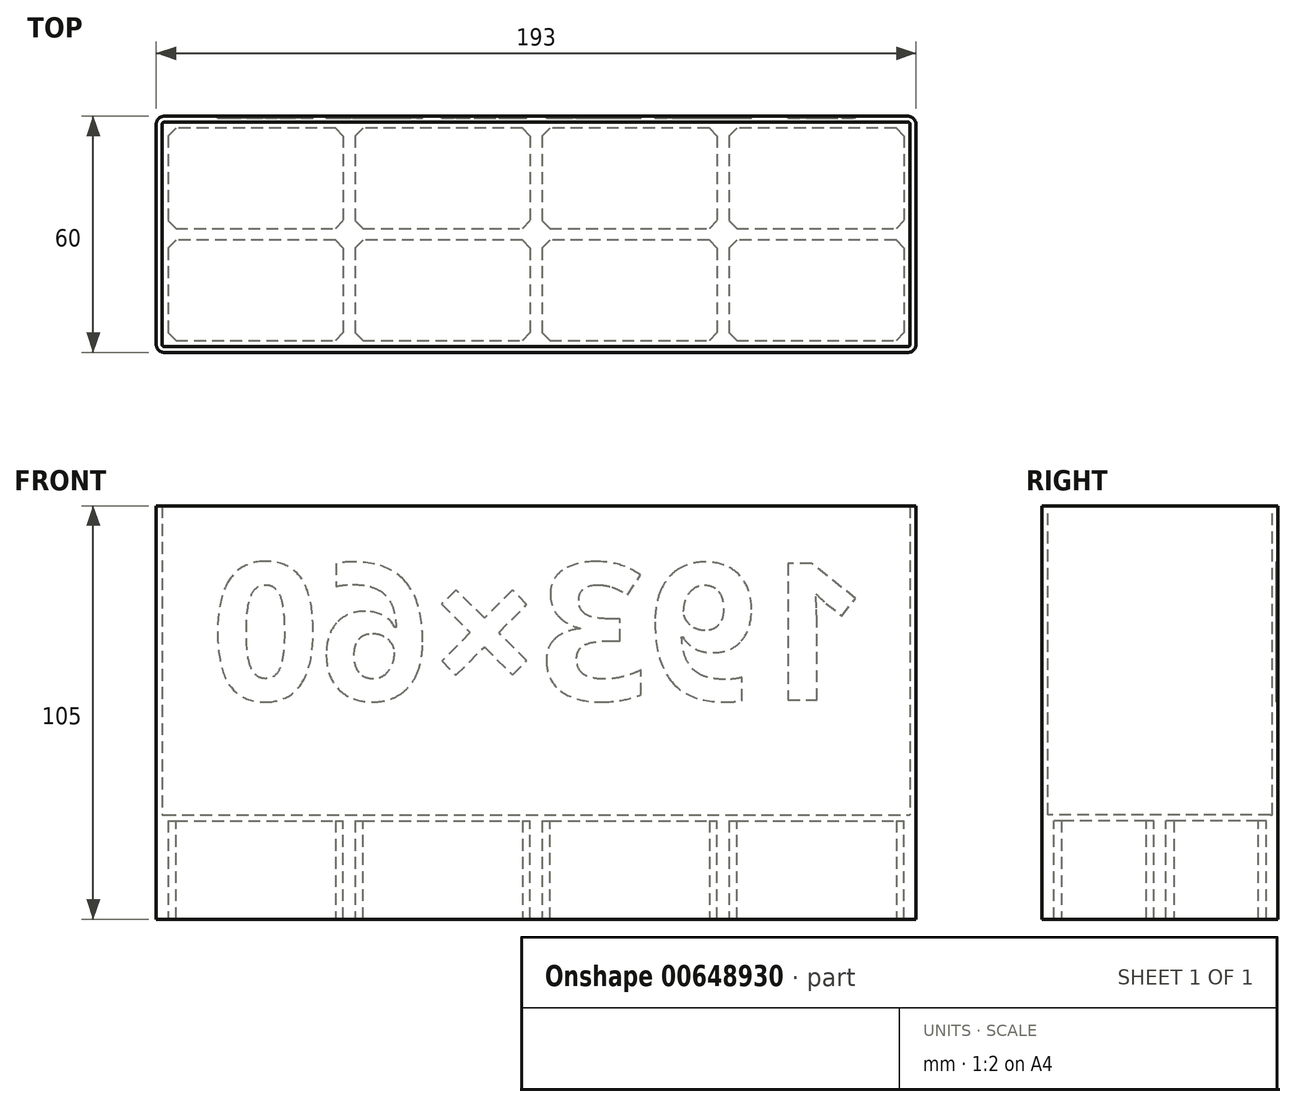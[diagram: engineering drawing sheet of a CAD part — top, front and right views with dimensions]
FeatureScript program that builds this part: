
annotation { "Feature Type Name" : "Feature", "Feature Type Description" : "" }
export const myFeature = defineFeature(function(context is Context, id is Id, definition is map)
    precondition{}
    {
        {
            assignVariable(context, id + "F0", {"variableType" : VariableType.LENGTH, "name" : "t", "lengthValue" : 1.5 * mm});
        }
        {
            assignVariable(context, id + "F1", {"variableType" : VariableType.LENGTH, "name" : "gap", "lengthValue" : 0.5 * mm});
        }
        {
            var Q0;
            Q0=qCreatedBy(makeId("Top.planeOp"),FACE);
            var sketch = newSketch(context, id + "F2", { "sketchPlane" : qUnion([Q0])});
            skLineSegment(sketch, "E0.bottom", {"start": v(-95, 28.5) * mm, "end": v(95, 28.5) * mm, "construction": true});
            skLineSegment(sketch, "E0.top", {"start": v(-95, -28.5) * mm, "end": v(95, -28.5) * mm, "construction": true});
            skLineSegment(sketch, "E0.left", {"start": v(-95, 28.5) * mm, "end": v(-95, -28.5) * mm, "construction": true});
            skLineSegment(sketch, "E0.right", {"start": v(95, 28.5) * mm, "end": v(95, -28.5) * mm, "construction": true});
            skPoint(sketch, "E0.middle", {"position": v(0, 0) * mm});
            skLineSegment(sketch, "E1.0", {"start": v(-96.5, 30) * mm, "end": v(96.5, 30) * mm});
            skLineSegment(sketch, "E1.1", {"start": v(-96.5, 30) * mm, "end": v(-96.5, -30) * mm});
            skLineSegment(sketch, "E1.2", {"start": v(-96.5, -30) * mm, "end": v(96.5, -30) * mm});
            skLineSegment(sketch, "E1.3", {"start": v(96.5, 30) * mm, "end": v(96.5, -30) * mm});
            skSolve(sketch);
        }
        {
            var Q0;
            Q0 = qSketchRegion(id + "F2", true);
            extrude(context, id + "F3", {"entities" : qUnion([Q0]), "depth" : 80 * mm, "offsetDistance" : 25 * mm});
        }
        {
            var Q0;
            Q0=makeQuery(id+"F3.opExtrude","CAP_FACE",FACE,{"disambiguationData":[OSD([sQuery(id+"F2.wireOp",EDGE,"E1.0"),sQuery(id+"F2.wireOp",EDGE,"E1.1"),sQuery(id+"F2.wireOp",EDGE,"E1.2"),sQuery(id+"F2.wireOp",EDGE,"E1.3")])],"isStart":true});
            var sketch = newSketch(context, id + "F4", { "sketchPlane" : qUnion([Q0])});
            skLineSegment(sketch, "E2.0", {"start": v(-95, 28.5) * mm, "end": v(-47.5, 28.5) * mm, "construction": true});
            skLineSegment(sketch, "E2.1", {"start": v(-95, -28.5) * mm, "end": v(-95, 0) * mm, "construction": true});
            skLineSegment(sketch, "E2.2", {"start": v(-95, -28.5) * mm, "end": v(95, -28.5) * mm, "construction": true});
            skLineSegment(sketch, "E2.3", {"start": v(95, -28.5) * mm, "end": v(95, 28.5) * mm, "construction": true});
            skLineSegment(sketch, "E3", {"start": v(0, 0) * mm, "end": v(0, 28.5) * mm, "construction": true});
            skLineSegment(sketch, "E4", {"start": v(0, 0) * mm, "end": v(-47.5, 0) * mm, "construction": true});
            skLineSegment(sketch, "E5", {"start": v(-47.5, 0) * mm, "end": v(-47.5, 28.5) * mm, "construction": true});
            skLineSegment(sketch, "E6", {"start": v(-47.5, 0) * mm, "end": v(-95, 0) * mm, "construction": true});
            skLineSegment(sketch, "E7", {"start": v(-47.5, 28.5) * mm, "end": v(95, 28.5) * mm, "construction": true});
            skLineSegment(sketch, "E8", {"start": v(-95, 0) * mm, "end": v(-95, 28.5) * mm, "construction": true});
            skLineSegment(sketch, "E9.0", {"start": v(-93.5, 27) * mm, "end": v(-49, 27) * mm});
            skLineSegment(sketch, "E9.1", {"start": v(-93.5, 1.5) * mm, "end": v(-93.5, 27) * mm});
            skLineSegment(sketch, "E9.2", {"start": v(-49, 1.5) * mm, "end": v(-93.5, 1.5) * mm});
            skLineSegment(sketch, "E9.3", {"start": v(-49, 1.5) * mm, "end": v(-49, 27) * mm});
            skLineSegment(sketch, "E10.0.1.0", {"start": v(-93.5, -1.5) * mm, "end": v(-49, -1.5) * mm});
            skLineSegment(sketch, "E10.0.1.1", {"start": v(-93.5, -27) * mm, "end": v(-93.5, -1.5) * mm});
            skLineSegment(sketch, "E10.0.1.2", {"start": v(-49, -27) * mm, "end": v(-93.5, -27) * mm});
            skLineSegment(sketch, "E10.0.1.3", {"start": v(-49, -27) * mm, "end": v(-49, -1.5) * mm});
            skLineSegment(sketch, "E10.1.0.0", {"start": v(-46, 27) * mm, "end": v(-1.5, 27) * mm});
            skLineSegment(sketch, "E10.1.0.1", {"start": v(-46, 1.5) * mm, "end": v(-46, 27) * mm});
            skLineSegment(sketch, "E10.1.0.2", {"start": v(-1.5, 1.5) * mm, "end": v(-46, 1.5) * mm});
            skLineSegment(sketch, "E10.1.0.3", {"start": v(-1.5, 1.5) * mm, "end": v(-1.5, 27) * mm});
            skLineSegment(sketch, "E10.1.1.0", {"start": v(-46, -1.5) * mm, "end": v(-1.5, -1.5) * mm});
            skLineSegment(sketch, "E10.1.1.1", {"start": v(-46, -27) * mm, "end": v(-46, -1.5) * mm});
            skLineSegment(sketch, "E10.1.1.2", {"start": v(-1.5, -27) * mm, "end": v(-46, -27) * mm});
            skLineSegment(sketch, "E10.1.1.3", {"start": v(-1.5, -27) * mm, "end": v(-1.5, -1.5) * mm});
            skLineSegment(sketch, "E10.2.0.0", {"start": v(1.5, 27) * mm, "end": v(46, 27) * mm});
            skLineSegment(sketch, "E10.2.0.1", {"start": v(1.5, 1.5) * mm, "end": v(1.5, 27) * mm});
            skLineSegment(sketch, "E10.2.0.2", {"start": v(46, 1.5) * mm, "end": v(1.5, 1.5) * mm});
            skLineSegment(sketch, "E10.2.0.3", {"start": v(46, 1.5) * mm, "end": v(46, 27) * mm});
            skLineSegment(sketch, "E10.2.1.0", {"start": v(1.5, -1.5) * mm, "end": v(46, -1.5) * mm});
            skLineSegment(sketch, "E10.2.1.1", {"start": v(1.5, -27) * mm, "end": v(1.5, -1.5) * mm});
            skLineSegment(sketch, "E10.2.1.2", {"start": v(46, -27) * mm, "end": v(1.5, -27) * mm});
            skLineSegment(sketch, "E10.2.1.3", {"start": v(46, -27) * mm, "end": v(46, -1.5) * mm});
            skLineSegment(sketch, "E10.3.0.0", {"start": v(49, 27) * mm, "end": v(93.5, 27) * mm});
            skLineSegment(sketch, "E10.3.0.1", {"start": v(49, 1.5) * mm, "end": v(49, 27) * mm});
            skLineSegment(sketch, "E10.3.0.2", {"start": v(93.5, 1.5) * mm, "end": v(49, 1.5) * mm});
            skLineSegment(sketch, "E10.3.0.3", {"start": v(93.5, 1.5) * mm, "end": v(93.5, 27) * mm});
            skLineSegment(sketch, "E10.3.1.0", {"start": v(49, -1.5) * mm, "end": v(93.5, -1.5) * mm});
            skLineSegment(sketch, "E10.3.1.1", {"start": v(49, -27) * mm, "end": v(49, -1.5) * mm});
            skLineSegment(sketch, "E10.3.1.2", {"start": v(93.5, -27) * mm, "end": v(49, -27) * mm});
            skLineSegment(sketch, "E10.3.1.3", {"start": v(93.5, -27) * mm, "end": v(93.5, -1.5) * mm});
            skLineSegment(sketch, "E10.direction1", {"start": v(-93.5, 1.5) * mm, "end": v(-46, 1.5) * mm, "construction": true});
            skLineSegment(sketch, "E10.direction2", {"start": v(-93.5, 1.5) * mm, "end": v(-93.5, -27) * mm, "construction": true});
            skLineSegment(sketch, "E11.bottom", {"start": v(-96.5, 30) * mm, "end": v(96.5, 30) * mm});
            skLineSegment(sketch, "E11.top", {"start": v(-96.5, -30) * mm, "end": v(96.5, -30) * mm});
            skLineSegment(sketch, "E11.left", {"start": v(-96.5, 30) * mm, "end": v(-96.5, -30) * mm});
            skLineSegment(sketch, "E11.right", {"start": v(96.5, 30) * mm, "end": v(96.5, -30) * mm});
            skSolve(sketch);
        }
        {
            var Q0;
            Q0=makeQuery(id+"F3.opExtrude","SWEPT_EDGE",EDGE,{"disambiguationData":[OSD([sQuery(id+"F2.wireOp",EDGE,"E1.1"),sQuery(id+"F2.wireOp",EDGE,"E1.2")])]});
            var Q1;
            Q1=makeQuery(id+"F3.opExtrude","SWEPT_EDGE",EDGE,{"disambiguationData":[OSD([sQuery(id+"F2.wireOp",EDGE,"E1.2"),sQuery(id+"F2.wireOp",EDGE,"E1.3")])]});
            var Q2;
            Q2=makeQuery(id+"F3.opExtrude","SWEPT_EDGE",EDGE,{"disambiguationData":[OSD([sQuery(id+"F2.wireOp",EDGE,"E1.0"),sQuery(id+"F2.wireOp",EDGE,"E1.3")])]});
            var Q3;
            Q3=makeQuery(id+"F3.opExtrude","SWEPT_EDGE",EDGE,{"disambiguationData":[OSD([sQuery(id+"F2.wireOp",EDGE,"E1.0"),sQuery(id+"F2.wireOp",EDGE,"E1.1")])]});
            fillet(context, id + "F5", {"entities" : qUnion([Q0, Q1, Q2, Q3]), "tangentPropagation" : true, "radius" : getVariable(context, 't') + getVariable(context, 'gap'), "defaultsChanged" : false, "vertexSettings" : [], "allowEdgeOverflow" : false});
        }
        {
            var Q0;
            Q0=makeQuery(id+"F3.opExtrude","CAP_FACE",FACE,{"disambiguationData":[OSD([sQuery(id+"F2.wireOp",EDGE,"E1.0"),sQuery(id+"F2.wireOp",EDGE,"E1.1"),sQuery(id+"F2.wireOp",EDGE,"E1.2"),sQuery(id+"F2.wireOp",EDGE,"E1.3")])],"isStart":false});
            shell(context, id + "F6", {"entities" : qUnion([Q0]), "thickness" : getVariable(context, 't')});
        }
        {
            var Q0;
            Q0 = qSketchRegion(id + "F4", true);
            extrude(context, id + "F7", {"entities" : qUnion([Q0]), "operationType" : NewBodyOperationType.ADD, "depth" : 25 * mm, "offsetDistance" : 25 * mm});
        }
        {
            var Q0;
            Q0=makeQuery(id+"F7.boolean.opBoolean","MERGE",FACE,{"derivedFrom":[makeQuery(id+"F3.opExtrude","SWEPT_FACE",FACE,{"disambiguationData":[OSD([sQuery(id+"F2.wireOp",EDGE,"E1.0")])]}),makeQuery(id+"F7.opExtrude","SWEPT_FACE",FACE,{"disambiguationData":[OSD([sQuery(id+"F4.wireOp",EDGE,"E11.top")])]})]});
            var sketch = newSketch(context, id + "F8", { "sketchPlane" : qUnion([Q0])});
            skText(sketch, "E12", { "text": "193×60", "fontName": "NotoSans-Bold.ttf"});
            const initialGuessF8  = {"E12": [-0.08406, 0.03067, 1, 0, 0.035]};
            skSetInitialGuess(sketch, initialGuessF8);
            skSolve(sketch);
        }
        {
            var Q0;
            Q0 = qSketchRegion(id + "F8", true);
            extrude(context, id + "F9", {"entities" : qUnion([Q0]), "operationType" : NewBodyOperationType.REMOVE, "oppositeDirection" : true, "depth" : getVariable(context, 't') * (1 / 3), "offsetDistance" : 25 * mm});
        }
        {
            var Q0;
            Q0=makeQuery(id+"F7.opExtrude","SWEPT_EDGE",EDGE,{"disambiguationData":[OSD([sQuery(id+"F4.wireOp",EDGE,"E11.bottom"),sQuery(id+"F4.wireOp",EDGE,"E11.left")])]});
            var Q1;
            Q1=makeQuery(id+"F7.opExtrude","SWEPT_EDGE",EDGE,{"disambiguationData":[OSD([sQuery(id+"F4.wireOp",EDGE,"E11.top"),sQuery(id+"F4.wireOp",EDGE,"E11.left")])]});
            var Q2;
            Q2=makeQuery(id+"F7.opExtrude","SWEPT_EDGE",EDGE,{"disambiguationData":[OSD([sQuery(id+"F4.wireOp",EDGE,"E11.bottom"),sQuery(id+"F4.wireOp",EDGE,"E11.right")])]});
            var Q3;
            Q3=makeQuery(id+"F7.opExtrude","SWEPT_EDGE",EDGE,{"disambiguationData":[OSD([sQuery(id+"F4.wireOp",EDGE,"E11.top"),sQuery(id+"F4.wireOp",EDGE,"E11.right")])]});
            fillet(context, id + "F10", {"entities" : qUnion([Q0, Q1, Q2, Q3]), "tangentPropagation" : true, "radius" : getVariable(context, 't') + getVariable(context, 'gap'), "defaultsChanged" : false, "vertexSettings" : [], "allowEdgeOverflow" : false});
        }
        {
            var Q0;
            Q0=makeQuery(id+"F7.opExtrude","SWEPT_EDGE",EDGE,{"disambiguationData":[OSD([sQuery(id+"F4.wireOp",EDGE,"E9.0"),sQuery(id+"F4.wireOp",EDGE,"E9.1")])]});
            var Q1;
            Q1=makeQuery(id+"F7.opExtrude","SWEPT_EDGE",EDGE,{"disambiguationData":[OSD([sQuery(id+"F4.wireOp",EDGE,"E9.0"),sQuery(id+"F4.wireOp",EDGE,"E9.3")])]});
            var Q2;
            Q2=makeQuery(id+"F7.opExtrude","SWEPT_EDGE",EDGE,{"disambiguationData":[OSD([sQuery(id+"F4.wireOp",EDGE,"E10.1.0.0"),sQuery(id+"F4.wireOp",EDGE,"E10.1.0.3")])]});
            var Q3;
            Q3=makeQuery(id+"F7.opExtrude","SWEPT_EDGE",EDGE,{"disambiguationData":[OSD([sQuery(id+"F4.wireOp",EDGE,"E10.0.1.0"),sQuery(id+"F4.wireOp",EDGE,"E10.0.1.3")])]});
            var Q4;
            Q4=makeQuery(id+"F7.opExtrude","SWEPT_EDGE",EDGE,{"disambiguationData":[OSD([sQuery(id+"F4.wireOp",EDGE,"E10.1.1.0"),sQuery(id+"F4.wireOp",EDGE,"E10.1.1.3")])]});
            var Q5;
            Q5=makeQuery(id+"F7.opExtrude","SWEPT_EDGE",EDGE,{"disambiguationData":[OSD([sQuery(id+"F4.wireOp",EDGE,"E10.2.0.0"),sQuery(id+"F4.wireOp",EDGE,"E10.2.0.3")])]});
            var Q6;
            Q6=makeQuery(id+"F7.opExtrude","SWEPT_EDGE",EDGE,{"disambiguationData":[OSD([sQuery(id+"F4.wireOp",EDGE,"E10.2.1.0"),sQuery(id+"F4.wireOp",EDGE,"E10.2.1.3")])]});
            var Q7;
            Q7=makeQuery(id+"F7.opExtrude","SWEPT_EDGE",EDGE,{"disambiguationData":[OSD([sQuery(id+"F4.wireOp",EDGE,"E10.3.1.0"),sQuery(id+"F4.wireOp",EDGE,"E10.3.1.3")])]});
            var Q8;
            Q8=makeQuery(id+"F7.opExtrude","SWEPT_EDGE",EDGE,{"disambiguationData":[OSD([sQuery(id+"F4.wireOp",EDGE,"E10.3.0.0"),sQuery(id+"F4.wireOp",EDGE,"E10.3.0.3")])]});
            var Q9;
            Q9=makeQuery(id+"F7.opExtrude","SWEPT_EDGE",EDGE,{"disambiguationData":[OSD([sQuery(id+"F4.wireOp",EDGE,"E9.1"),sQuery(id+"F4.wireOp",EDGE,"E9.2")])]});
            var Q10;
            Q10=makeQuery(id+"F7.opExtrude","SWEPT_EDGE",EDGE,{"disambiguationData":[OSD([sQuery(id+"F4.wireOp",EDGE,"E10.0.1.1"),sQuery(id+"F4.wireOp",EDGE,"E10.0.1.2")])]});
            var Q11;
            Q11=makeQuery(id+"F7.opExtrude","SWEPT_EDGE",EDGE,{"disambiguationData":[OSD([sQuery(id+"F4.wireOp",EDGE,"E10.1.1.1"),sQuery(id+"F4.wireOp",EDGE,"E10.1.1.2")])]});
            var Q12;
            Q12=makeQuery(id+"F7.opExtrude","SWEPT_EDGE",EDGE,{"disambiguationData":[OSD([sQuery(id+"F4.wireOp",EDGE,"E10.2.1.1"),sQuery(id+"F4.wireOp",EDGE,"E10.2.1.2")])]});
            var Q13;
            Q13=makeQuery(id+"F7.opExtrude","SWEPT_EDGE",EDGE,{"disambiguationData":[OSD([sQuery(id+"F4.wireOp",EDGE,"E10.3.1.1"),sQuery(id+"F4.wireOp",EDGE,"E10.3.1.2")])]});
            var Q14;
            Q14=makeQuery(id+"F7.opExtrude","SWEPT_EDGE",EDGE,{"disambiguationData":[OSD([sQuery(id+"F4.wireOp",EDGE,"E10.3.0.1"),sQuery(id+"F4.wireOp",EDGE,"E10.3.0.2")])]});
            var Q15;
            Q15=makeQuery(id+"F7.opExtrude","SWEPT_EDGE",EDGE,{"disambiguationData":[OSD([sQuery(id+"F4.wireOp",EDGE,"E10.2.0.1"),sQuery(id+"F4.wireOp",EDGE,"E10.2.0.2")])]});
            var Q16;
            Q16=makeQuery(id+"F7.opExtrude","SWEPT_EDGE",EDGE,{"disambiguationData":[OSD([sQuery(id+"F4.wireOp",EDGE,"E10.1.0.1"),sQuery(id+"F4.wireOp",EDGE,"E10.1.0.2")])]});
            var Q17;
            Q17=makeQuery(id+"F7.opExtrude","SWEPT_EDGE",EDGE,{"disambiguationData":[OSD([sQuery(id+"F4.wireOp",EDGE,"E9.2"),sQuery(id+"F4.wireOp",EDGE,"E9.3")])]});
            var Q18;
            Q18=makeQuery(id+"F7.opExtrude","SWEPT_EDGE",EDGE,{"disambiguationData":[OSD([sQuery(id+"F4.wireOp",EDGE,"E10.1.0.2"),sQuery(id+"F4.wireOp",EDGE,"E10.1.0.3")])]});
            var Q19;
            Q19=makeQuery(id+"F7.opExtrude","SWEPT_EDGE",EDGE,{"disambiguationData":[OSD([sQuery(id+"F4.wireOp",EDGE,"E10.2.0.2"),sQuery(id+"F4.wireOp",EDGE,"E10.2.0.3")])]});
            var Q20;
            Q20=makeQuery(id+"F7.opExtrude","SWEPT_EDGE",EDGE,{"disambiguationData":[OSD([sQuery(id+"F4.wireOp",EDGE,"E10.3.0.2"),sQuery(id+"F4.wireOp",EDGE,"E10.3.0.3")])]});
            var Q21;
            Q21=makeQuery(id+"F7.opExtrude","SWEPT_EDGE",EDGE,{"disambiguationData":[OSD([sQuery(id+"F4.wireOp",EDGE,"E10.3.1.2"),sQuery(id+"F4.wireOp",EDGE,"E10.3.1.3")])]});
            var Q22;
            Q22=makeQuery(id+"F7.opExtrude","SWEPT_EDGE",EDGE,{"disambiguationData":[OSD([sQuery(id+"F4.wireOp",EDGE,"E10.2.1.2"),sQuery(id+"F4.wireOp",EDGE,"E10.2.1.3")])]});
            var Q23;
            Q23=makeQuery(id+"F7.opExtrude","SWEPT_EDGE",EDGE,{"disambiguationData":[OSD([sQuery(id+"F4.wireOp",EDGE,"E10.1.1.2"),sQuery(id+"F4.wireOp",EDGE,"E10.1.1.3")])]});
            var Q24;
            Q24=makeQuery(id+"F7.opExtrude","SWEPT_EDGE",EDGE,{"disambiguationData":[OSD([sQuery(id+"F4.wireOp",EDGE,"E10.0.1.2"),sQuery(id+"F4.wireOp",EDGE,"E10.0.1.3")])]});
            var Q25;
            Q25=makeQuery(id+"F7.opExtrude","SWEPT_EDGE",EDGE,{"disambiguationData":[OSD([sQuery(id+"F4.wireOp",EDGE,"E10.1.1.0"),sQuery(id+"F4.wireOp",EDGE,"E10.1.1.1")])]});
            var Q26;
            Q26=makeQuery(id+"F7.opExtrude","SWEPT_EDGE",EDGE,{"disambiguationData":[OSD([sQuery(id+"F4.wireOp",EDGE,"E10.0.1.0"),sQuery(id+"F4.wireOp",EDGE,"E10.0.1.1")])]});
            var Q27;
            Q27=makeQuery(id+"F7.opExtrude","SWEPT_EDGE",EDGE,{"disambiguationData":[OSD([sQuery(id+"F4.wireOp",EDGE,"E10.2.1.0"),sQuery(id+"F4.wireOp",EDGE,"E10.2.1.1")])]});
            var Q28;
            Q28=makeQuery(id+"F7.opExtrude","SWEPT_EDGE",EDGE,{"disambiguationData":[OSD([sQuery(id+"F4.wireOp",EDGE,"E10.3.1.0"),sQuery(id+"F4.wireOp",EDGE,"E10.3.1.1")])]});
            var Q29;
            Q29=makeQuery(id+"F7.opExtrude","SWEPT_EDGE",EDGE,{"disambiguationData":[OSD([sQuery(id+"F4.wireOp",EDGE,"E10.2.0.0"),sQuery(id+"F4.wireOp",EDGE,"E10.2.0.1")])]});
            var Q30;
            Q30=makeQuery(id+"F7.opExtrude","SWEPT_EDGE",EDGE,{"disambiguationData":[OSD([sQuery(id+"F4.wireOp",EDGE,"E10.3.0.0"),sQuery(id+"F4.wireOp",EDGE,"E10.3.0.1")])]});
            var Q31;
            Q31=makeQuery(id+"F7.opExtrude","SWEPT_EDGE",EDGE,{"disambiguationData":[OSD([sQuery(id+"F4.wireOp",EDGE,"E10.1.0.0"),sQuery(id+"F4.wireOp",EDGE,"E10.1.0.1")])]});
            chamfer(context, id + "F11", {"entities" : qUnion([Q0, Q1, Q2, Q3, Q4, Q5, Q6, Q7, Q8, Q9, Q10, Q11, Q12, Q13, Q14, Q15, Q16, Q17, Q18, Q19, Q20, Q21, Q22, Q23, Q24, Q25, Q26, Q27, Q28, Q29, Q30, Q31]), "width" : getVariable(context, 't') + getVariable(context, 'gap'), "tangentPropagation" : true});
        }
    });
